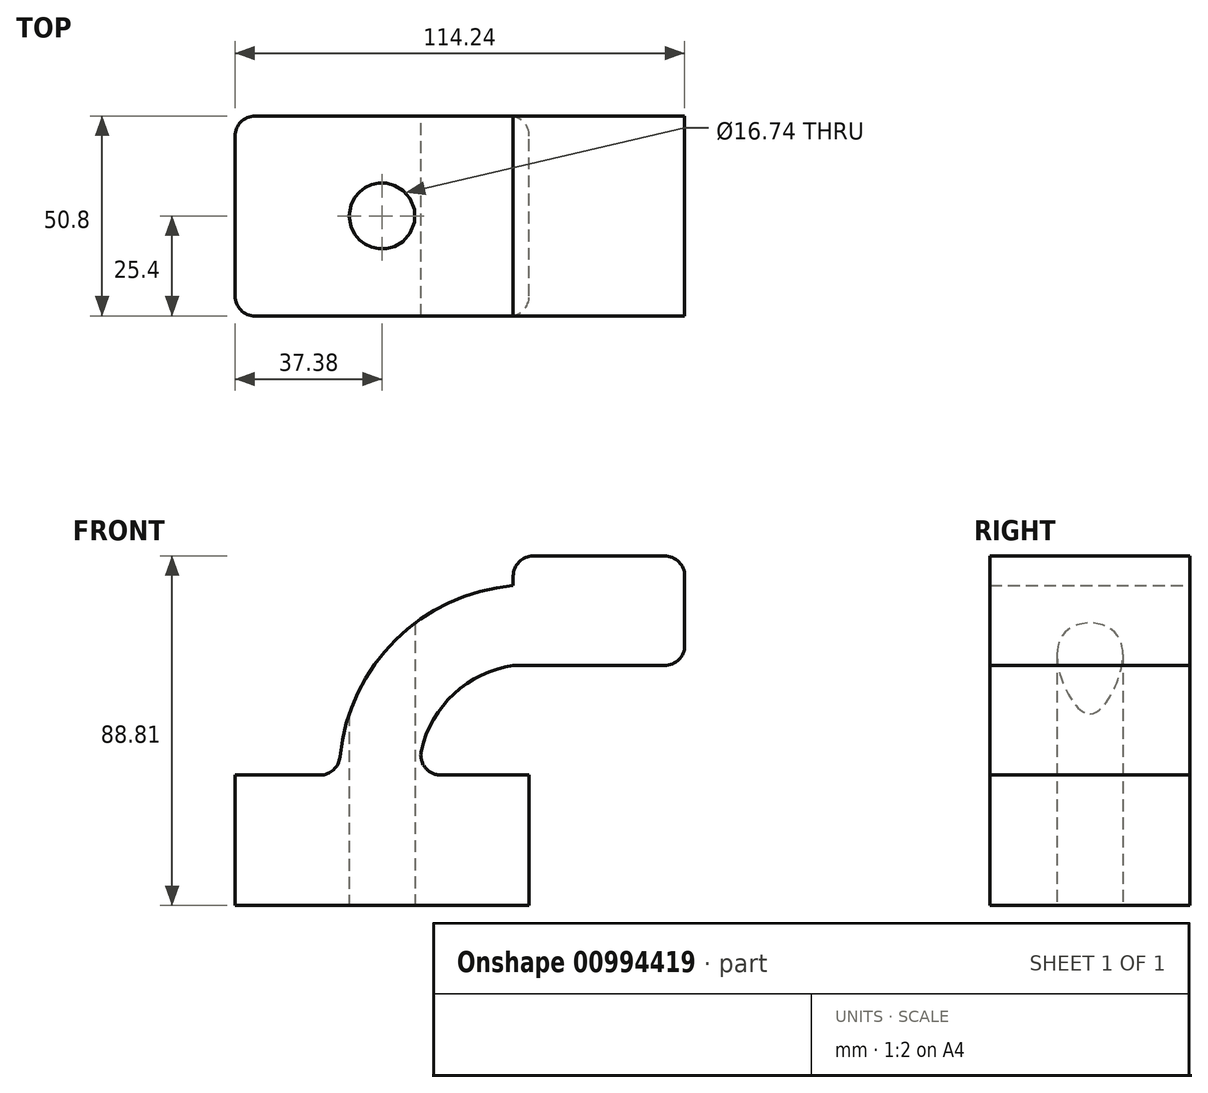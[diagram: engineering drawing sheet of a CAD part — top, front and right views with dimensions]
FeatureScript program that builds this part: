
annotation { "Feature Type Name" : "Feature", "Feature Type Description" : "" }
export const myFeature = defineFeature(function(context is Context, id is Id, definition is map)
    precondition{}
    {
        {
            var Q0;
            Q0=qCreatedBy(makeId("Front.planeOp"),FACE);
            var sketch = newSketch(context, id + "F0", { "sketchPlane" : qUnion([Q0])});
            skLineSegment(sketch, "E0.bottom", {"start": v(37.38, 16.58) * mm, "end": v(-37.38, 16.58) * mm});
            skLineSegment(sketch, "E0.top", {"start": v(37.38, -16.58) * mm, "end": v(-37.38, -16.58) * mm});
            skLineSegment(sketch, "E0.left", {"start": v(37.38, 16.58) * mm, "end": v(37.38, -16.58) * mm});
            skLineSegment(sketch, "E0.right", {"start": v(-37.38, 16.58) * mm, "end": v(-37.38, -16.58) * mm});
            skPoint(sketch, "E0.middle", {"position": v(0, 0) * mm});
            skLineSegment(sketch, "E1.bottom", {"start": v(76.86, 44.4) * mm, "end": v(33.31, 44.4) * mm});
            skLineSegment(sketch, "E1.top", {"start": v(76.86, 72.23) * mm, "end": v(33.31, 72.23) * mm});
            skLineSegment(sketch, "E1.left", {"start": v(76.86, 44.4) * mm, "end": v(76.86, 72.23) * mm});
            skLineSegment(sketch, "E1.right", {"start": v(33.31, 44.4) * mm, "end": v(33.31, 72.23) * mm});
            skPoint(sketch, "E1.middle", {"position": v(55.09, 58.32) * mm});
            skArc(sketch, "E2", {"start": v(33.31, 44.4) * mm, "mid": v(16.1, 34.97) * mm, "end": v(9.26, 16.58) * mm});
            skArc(sketch, "E3", {"start": v(76.86, 44.4) * mm, "mid": v(22.78, 62.63) * mm, "end": v(-10.92, 16.58) * mm});
            skSolve(sketch);
        }
        {
            var Q0;
            Q0=makeQuery(id+"F0.imprint","IMPRINT",FACE,{"disambiguationData":[TD([[makeQuery(id+"F0.imprint","IMPRINT",EDGE,{"derivedFrom":sQuery(id+"F0.wireOp",EDGE,"E0.top")}),-1.0]])]});
            var Q1;
            {var subQ0=sQuery(id+"F0.wireOp",EDGE,"E2");Q1=makeQuery(id+"F0.imprint","IMPRINT",FACE,{"disambiguationData":[TD([[makeQuery(id+"F0.imprint","IMPRINT",EDGE,{"derivedFrom":subQ0}),-1.0]])]});}
            var Q2;
            {var subQ0=sQuery(id+"F0.wireOp",EDGE,"E1.top");Q2=makeQuery(id+"F0.imprint","IMPRINT",FACE,{"disambiguationData":[TD([[makeQuery(id+"F0.imprint","IMPRINT",EDGE,{"derivedFrom":subQ0}),1.0]])]});}
            var Q3;
            {var subQ0=sQuery(id+"F0.wireOp",EDGE,"E1.bottom");Q3=makeQuery(id+"F0.imprint","IMPRINT",FACE,{"disambiguationData":[TD([[makeQuery(id+"F0.imprint","IMPRINT",EDGE,{"derivedFrom":subQ0}),-1.0]])]});}
            extrude(context, id + "F1", {"entities" : qUnion([Q0, Q1, Q2, Q3]), "depth" : 50.8 * mm, "offsetDistance" : 25.4 * mm, "symmetric" : true});
        }
        {
            var Q0;
            Q0=makeQuery(id+"F1.opExtrude","CAP_EDGE",EDGE,{"disambiguationData":[OSD([sQuery(id+"F0.wireOp",EDGE,"E0.right")])],"isStart":false});
            var Q1;
            Q1=makeQuery(id+"F1.opExtrude","CAP_EDGE",EDGE,{"disambiguationData":[OSD([sQuery(id+"F0.wireOp",EDGE,"E0.left")])],"isStart":false});
            var Q2;
            Q2=makeQuery(id+"F1.opExtrude","CAP_EDGE",EDGE,{"disambiguationData":[OSD([sQuery(id+"F0.wireOp",EDGE,"E0.left")])],"isStart":true});
            var Q3;
            Q3=makeQuery(id+"F1.opExtrude","CAP_EDGE",EDGE,{"disambiguationData":[OSD([sQuery(id+"F0.wireOp",EDGE,"E0.right")])],"isStart":true});
            fillet(context, id + "F2", {"entities" : qUnion([Q0, Q1, Q2, Q3]), "radius" : 5.08 * mm, "tangentPropagation" : true, "allowEdgeOverflow" : false});
        }
        {
            var Q0;
            Q0=makeQuery(id+"F1.opExtrude","SWEPT_EDGE",EDGE,{"disambiguationData":[OSD([sQuery(id+"F0.wireOp",EDGE,"E0.bottom"),sQuery(id+"F0.wireOp",EDGE,"E2")])]});
            var Q1;
            Q1=makeQuery(id+"F1.opExtrude","SWEPT_EDGE",EDGE,{"disambiguationData":[OSD([sQuery(id+"F0.wireOp",EDGE,"E0.bottom"),sQuery(id+"F0.wireOp",EDGE,"E3")])]});
            var Q2;
            Q2=makeQuery(id+"F1.opExtrude","SWEPT_EDGE",EDGE,{"disambiguationData":[OSD([sQuery(id+"F0.wireOp",EDGE,"E1.top"),sQuery(id+"F0.wireOp",EDGE,"E1.right")])]});
            var Q3;
            Q3=makeQuery(id+"F1.opExtrude","SWEPT_EDGE",EDGE,{"disambiguationData":[OSD([sQuery(id+"F0.wireOp",EDGE,"E1.top"),sQuery(id+"F0.wireOp",EDGE,"E1.left")])]});
            var Q4;
            Q4=makeQuery(id+"F1.opExtrude","SWEPT_EDGE",EDGE,{"disambiguationData":[OSD([sQuery(id+"F0.wireOp",EDGE,"E1.bottom"),sQuery(id+"F0.wireOp",EDGE,"E1.left"),sQuery(id+"F0.wireOp",EDGE,"E3")])]});
            fillet(context, id + "F3", {"entities" : qUnion([Q0, Q1, Q2, Q3, Q4]), "radius" : 5.08 * mm, "tangentPropagation" : true, "allowEdgeOverflow" : false});
        }
        {
            var Q0;
            Q0=makeQuery(id+"F1.opExtrude","SWEPT_FACE",FACE,{"disambiguationData":[OSD([sQuery(id+"F0.wireOp",EDGE,"E0.top")])]});
            var sketch = newSketch(context, id + "F4", { "sketchPlane" : qUnion([Q0])});
            skCircle(sketch, "E4", {"center": v(0, 0) * mm, "radius": 8.37 * mm});
            skSolve(sketch);
        }
        {
            var Q0;
            Q0 = qSketchRegion(id + "F4", true);
            extrude(context, id + "F5", {"entities" : qUnion([Q0]), "operationType" : NewBodyOperationType.REMOVE, "oppositeDirection" : true, "depth" : 99.31 * mm, "offsetDistance" : 25.4 * mm});
        }
    });
